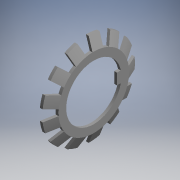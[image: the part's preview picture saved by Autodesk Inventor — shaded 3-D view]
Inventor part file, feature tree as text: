
AUTODESK INVENTOR PART (.ipt)
format: ipt  version: 2017.3 (Build 213256000, 256)  size: 221,696 bytes
history: native  units: mm (DEFAULTED — no unit token found)
features: other x21, sketch x3, extrude x2, revolve x1
ambient origin geometry x8: Origin, YZ Plane, XZ Plane, XY Plane, X Axis, Y Axis, Z Axis, Center Point
bodies: Solid1 (feature_tree)
feature tree (27):
  revolve  "Revolution1"  [1 undecoded]
  extrude  "Extrusion1"  TaperAngle=0.0deg  [1 undecoded]
  extrude  "Extrusion2"  [1 undecoded]
  other  "mb_XY"
  other  "mb_YZ"
  other  "mb_ZX"
  other  "mb_X"
  other  "mb_Y"
  other  "mb_Z"
  other  "mb_Center"
  other  "mb2_XY"
  other  "mb2_YZ"
  other  "mb2_ZX"
  other  "mb2_X"
  other  "mb2_Y"
  other  "mb2_Z"
  other  "mb2_Center"
  other  "to_locknut_XY"
  other  "to_locknut_YZ"
  other  "to_locknut_ZX"
  other  "to_locknut_X"
  other  "to_locknut_Y"
  other  "to_locknut_Z"
  other  "to_locknut_Center"
  sketch  "Sketch_1"  dims[d0=360.0deg d1=25.0mm d2=0.0mm]
  sketch  "Sketch_2"  dims[d3=1.25mm d4=0.0mm d5=0.0mm]
  sketch  "Sketch_7"
note: 3 required parameter values undecoded (feature->parameter linkage not recoverable at this tier; creation-order binding heuristic only, values carry confidence <= 0.55)